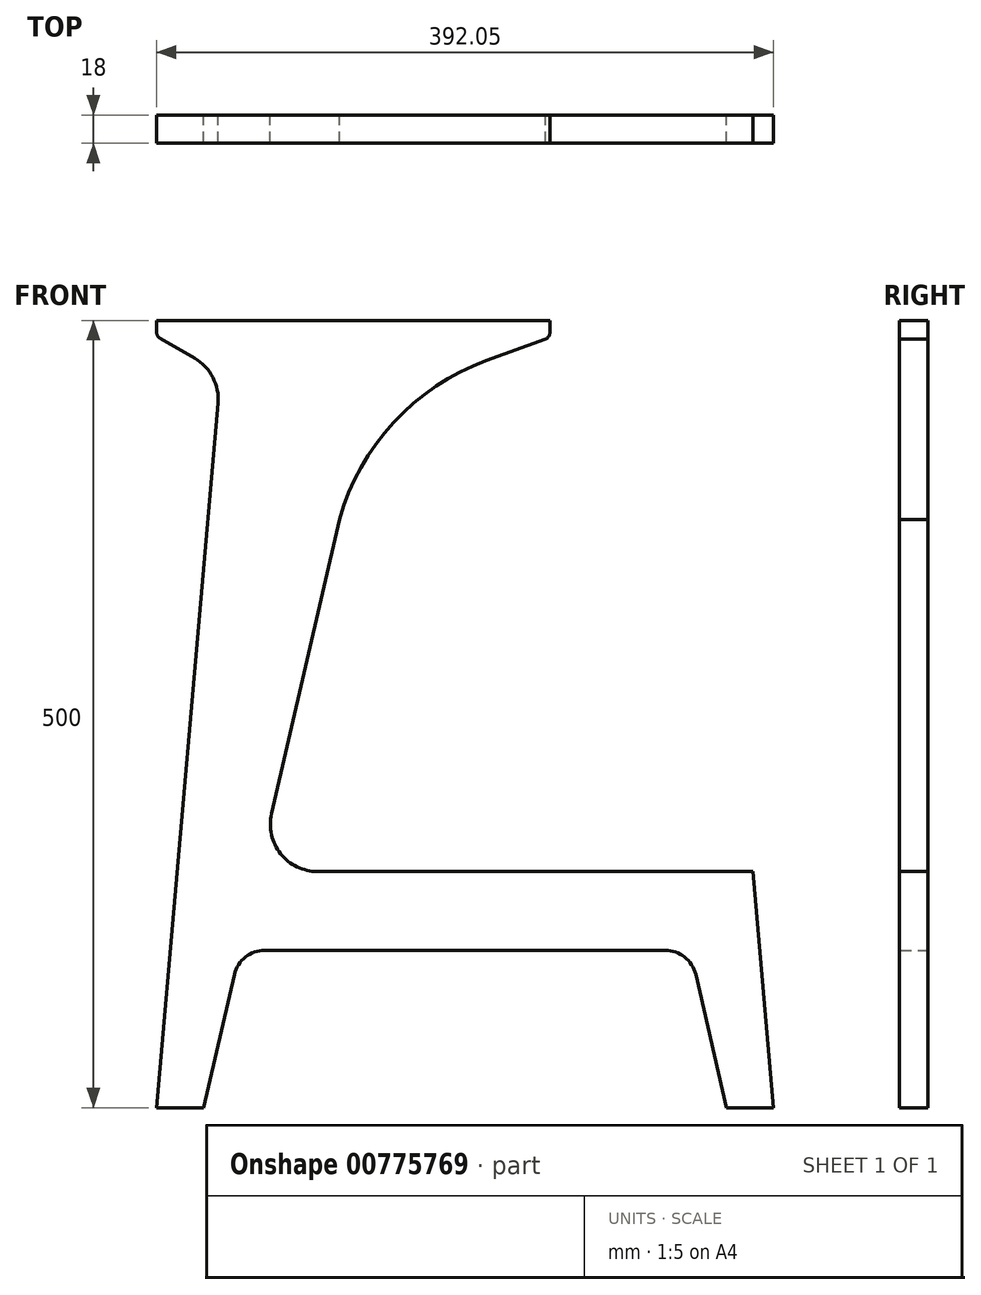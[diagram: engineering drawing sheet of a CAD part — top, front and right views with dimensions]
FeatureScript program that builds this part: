
annotation { "Feature Type Name" : "Feature", "Feature Type Description" : "" }
export const myFeature = defineFeature(function(context is Context, id is Id, definition is map)
    precondition{}
    {
        {
            var Q0;
            Q0=qCreatedBy(makeId("Front.planeOp"),FACE);
            var sketch = newSketch(context, id + "F0", { "sketchPlane" : qUnion([Q0])});
            skLineSegment(sketch, "E0", {"start": v(30, 0) * mm, "end": v(0, 0) * mm});
            skLineSegment(sketch, "E1", {"start": v(0, 0) * mm, "end": v(0, 150) * mm});
            skLineSegment(sketch, "E2", {"start": v(0, 500) * mm, "end": v(250, 500) * mm});
            skPoint(sketch, "E3", {"position": v(0, 150) * mm});
            skPoint(sketch, "E4.endSnap0", {"position": v(116.58, 245.6) * mm});
            skLineSegment(sketch, "E5", {"start": v(250, 500) * mm, "end": v(250, 492.64) * mm});
            skPoint(sketch, "E6.orphan", {"position": v(203.17, 491.2) * mm});
            skLineSegment(sketch, "E7", {"start": v(102.35, 150) * mm, "end": v(378.92, 150) * mm});
            skPoint(sketch, "E8.orphan", {"position": v(100, 198.56) * mm});
            skLineSegment(sketch, "E9", {"start": v(116.26, 373.62) * mm, "end": v(73.11, 186.75) * mm});
            skLineSegment(sketch, "E10", {"start": v(362.05, 0) * mm, "end": v(392.05, 0) * mm});
            skLineSegment(sketch, "E11", {"start": v(392.05, 0) * mm, "end": v(378.92, 150) * mm});
            skLineSegment(sketch, "E12", {"start": v(69, 100) * mm, "end": v(323.05, 100) * mm});
            skLineSegment(sketch, "E13.trimOffspring", {"start": v(49.5, 84.5) * mm, "end": v(30, 0) * mm});
            skLineSegment(sketch, "E14", {"start": v(392.05, 0) * mm, "end": v(362.05, 0) * mm});
            skLineSegment(sketch, "E15", {"start": v(362.05, 0) * mm, "end": v(342.54, 84.5) * mm});
            skPoint(sketch, "E16.visualSharp", {"position": v(130.88, 436.96) * mm});
            skPoint(sketch, "E17.visualSharp", {"position": v(250, 466.54) * mm});
            skPoint(sketch, "E18.visualSharp", {"position": v(64.63, 150) * mm});
            skArc(sketch, "E18.filletArc", {"start": v(73.11, 186.75) * mm, "mid": v(78.87, 161.32) * mm, "end": v(102.35, 150) * mm});
            skPoint(sketch, "E19.visualSharp", {"position": v(338.96, 100) * mm});
            skArc(sketch, "E19.filletArc", {"start": v(342.54, 84.5) * mm, "mid": v(335.5, 95.65) * mm, "end": v(323.05, 100) * mm});
            skPoint(sketch, "E20.visualSharp", {"position": v(53.09, 100) * mm});
            skArc(sketch, "E20.filletArc", {"start": v(69, 100) * mm, "mid": v(56.55, 95.65) * mm, "end": v(49.5, 84.5) * mm});
            skLineSegment(sketch, "E21", {"start": v(0, 0) * mm, "end": v(37.08, 423.86) * mm});
            skLineSegment(sketch, "E22", {"start": v(0, 500) * mm, "end": v(0, 492.89) * mm});
            skLineSegment(sketch, "E23.trimOffspring", {"start": v(0, 490) * mm, "end": v(0, 500) * mm});
            skPoint(sketch, "E24.trimOffspring.end.orphan", {"position": v(-77.5, 432.13) * mm});
            skPoint(sketch, "E25.newPointA", {"position": v(38.62, 436.77) * mm});
            skLineSegment(sketch, "E26", {"start": v(2.5, 488.56) * mm, "end": v(24.26, 476) * mm});
            skLineSegment(sketch, "E27", {"start": v(37.08, 423.86) * mm, "end": v(39.14, 447.4) * mm});
            skPoint(sketch, "E28.visualSharp", {"position": v(126.69, 418.8) * mm});
            skPoint(sketch, "E29.visualSharp", {"position": v(40.8, 466.44) * mm});
            skArc(sketch, "E29.filletArc", {"start": v(39.14, 447.4) * mm, "mid": v(35.87, 463.87) * mm, "end": v(24.26, 476) * mm});
            skPoint(sketch, "E30.visualSharp", {"position": v(0, 490) * mm});
            skArc(sketch, "E30.filletArc", {"start": v(0, 492.89) * mm, "mid": v(0.67, 490.39) * mm, "end": v(2.5, 488.56) * mm});
            skPoint(sketch, "E31.visualSharp", {"position": v(250, 490) * mm});
            skArc(sketch, "E31.filletArc", {"start": v(247.06, 488.08) * mm, "mid": v(249.2, 489.93) * mm, "end": v(250, 492.64) * mm});
            skLineSegment(sketch, "E32", {"start": v(247.06, 488.08) * mm, "end": v(209.47, 474.4) * mm});
            skArc(sketch, "E33", {"start": v(209.47, 474.4) * mm, "mid": v(150.66, 435.3) * mm, "end": v(116.26, 373.62) * mm});
            skSolve(sketch);
        }
        {
            var Q0;
            Q0=makeQuery(id+"F0.imprint","IMPRINT",FACE,{"disambiguationData":[TD([[makeQuery(id+"F0.imprint","IMPRINT",EDGE,{"derivedFrom":sQuery(id+"F0.wireOp",EDGE,"E0")}),-1.0]])]});
            extrude(context, id + "F1", {"entities" : qUnion([Q0]), "depth" : 18 * mm, "offsetDistance" : 25 * mm});
        }
    });
